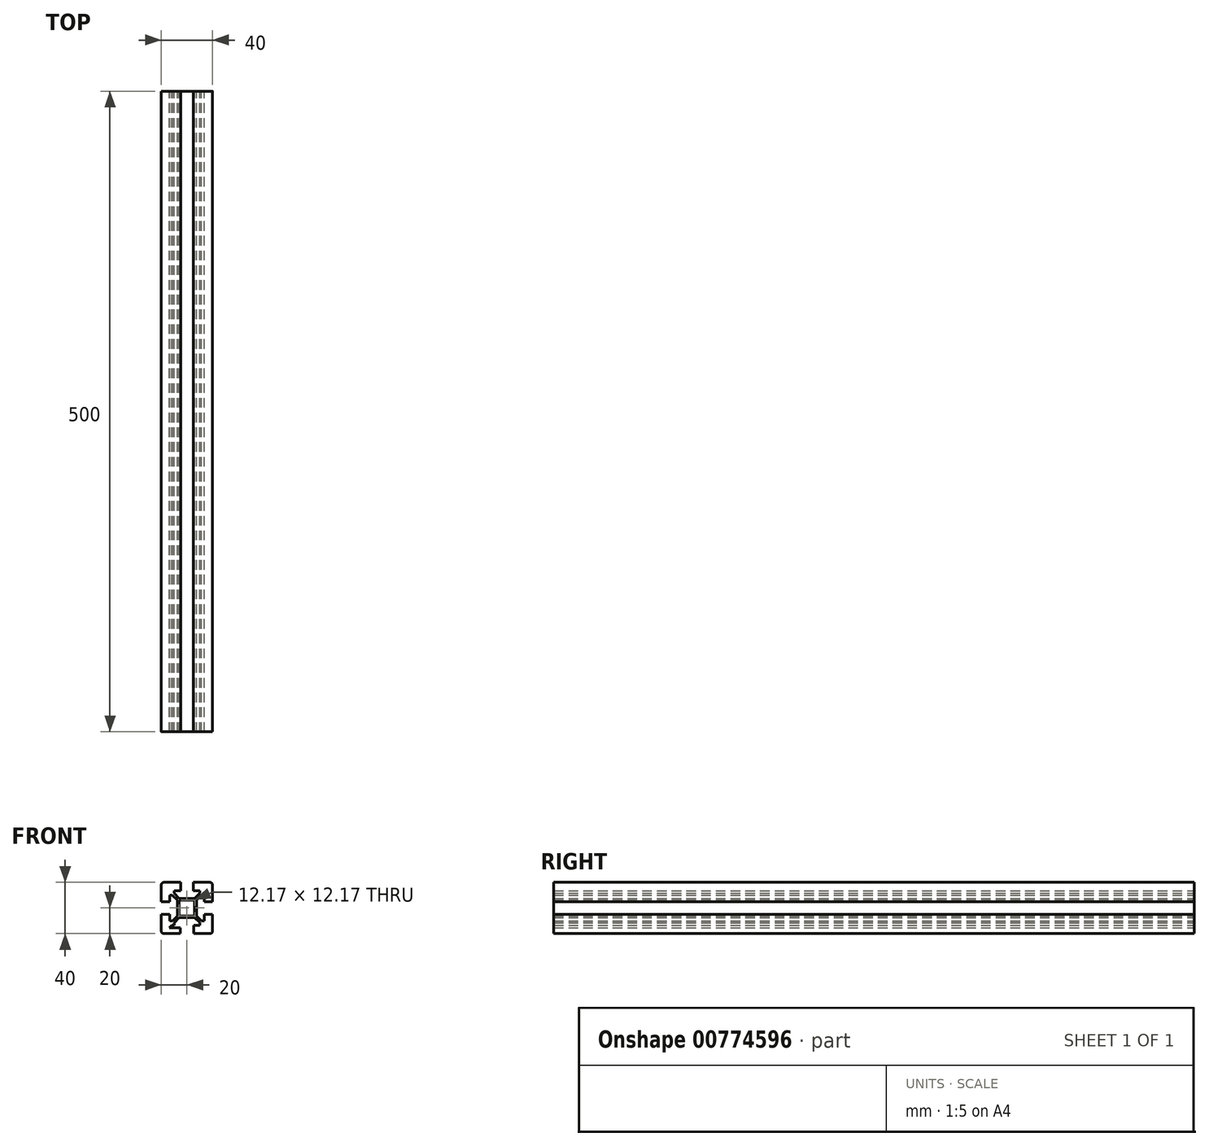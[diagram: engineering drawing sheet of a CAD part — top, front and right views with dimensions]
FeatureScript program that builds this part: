
annotation { "Feature Type Name" : "Feature", "Feature Type Description" : "" }
export const myFeature = defineFeature(function(context is Context, id is Id, definition is map)
    precondition{}
    {
        {
            var Q0;
            Q0=qCreatedBy(makeId("Front.planeOp"),FACE);
            var sketch = newSketch(context, id + "F0", { "sketchPlane" : qUnion([Q0])});
            skLineSegment(sketch, "E0.bottom", {"start": v(18, -20) * mm, "end": v(5.2, -20) * mm});
            skLineSegment(sketch, "E0.top", {"start": v(18, 20) * mm, "end": v(5, 20) * mm});
            skLineSegment(sketch, "E0.left", {"start": v(20, -18) * mm, "end": v(20, -5) * mm});
            skLineSegment(sketch, "E0.right", {"start": v(-20, -18) * mm, "end": v(-20, -5) * mm});
            skPoint(sketch, "E0.middle", {"position": v(0, 0) * mm});
            skLineSegment(sketch, "E1.bottom", {"start": v(16.63, -17.93) * mm, "end": v(5.2, -17.93) * mm});
            skLineSegment(sketch, "E1.top", {"start": v(16.58, 17.93) * mm, "end": v(5.15, 17.93) * mm});
            skLineSegment(sketch, "E1.left", {"start": v(18.05, -16.6) * mm, "end": v(18.05, -5.01) * mm});
            skLineSegment(sketch, "E1.right", {"start": v(-18.05, -16.9) * mm, "end": v(-18.05, -5.01) * mm});
            skLineSegment(sketch, "E2.bottom", {"start": v(5.5, -5.5) * mm, "end": v(-5.5, -5.5) * mm});
            skLineSegment(sketch, "E2.top", {"start": v(5.5, 5.5) * mm, "end": v(-5.5, 5.5) * mm});
            skLineSegment(sketch, "E2.left", {"start": v(5.5, -5.5) * mm, "end": v(5.5, 5.5) * mm});
            skLineSegment(sketch, "E2.right", {"start": v(-5.5, -5.5) * mm, "end": v(-5.5, 5.5) * mm});
            skLineSegment(sketch, "E3.bottom", {"start": v(6.09, -7.52) * mm, "end": v(-6.06, -7.52) * mm});
            skLineSegment(sketch, "E3.top", {"start": v(6.09, 7.52) * mm, "end": v(-6.09, 7.52) * mm});
            skLineSegment(sketch, "E3.left", {"start": v(7.48, -6.09) * mm, "end": v(7.48, 6.09) * mm});
            skLineSegment(sketch, "E3.right", {"start": v(-7.48, -6.12) * mm, "end": v(-7.48, 6.09) * mm});
            skPoint(sketch, "E4.middle", {"position": v(-20, 0) * mm});
            skLineSegment(sketch, "E5.left", {"start": v(5.2, -17.93) * mm, "end": v(5.2, -20) * mm});
            skLineSegment(sketch, "E5.right", {"start": v(-5.2, -17.93) * mm, "end": v(-5.2, -20) * mm});
            skPoint(sketch, "E5.middle", {"position": v(0, -20) * mm});
            skPoint(sketch, "E6.middle", {"position": v(20, 0) * mm});
            skPoint(sketch, "E7.middle", {"position": v(0, 20) * mm});
            skLineSegment(sketch, "E8.trimOffspring", {"start": v(-20, 5) * mm, "end": v(-20, 18) * mm});
            skLineSegment(sketch, "E9.trimOffspring", {"start": v(-18.05, 4.99) * mm, "end": v(-18.05, 10) * mm});
            skPoint(sketch, "E10.orphan", {"position": v(-21.95, 5.01) * mm});
            skPoint(sketch, "E11.orphan", {"position": v(-21.95, -4.99) * mm});
            skLineSegment(sketch, "E12.trimOffspring", {"start": v(-5, 20) * mm, "end": v(-18, 20) * mm});
            skLineSegment(sketch, "E13.trimOffspring", {"start": v(-4.85, 17.93) * mm, "end": v(-10, 17.93) * mm});
            skPoint(sketch, "E14.orphan", {"position": v(4.85, 22.07) * mm});
            skPoint(sketch, "E15.orphan", {"position": v(-5.15, 22.07) * mm});
            skLineSegment(sketch, "E16.trimOffspring", {"start": v(20, 5) * mm, "end": v(20, 18) * mm});
            skLineSegment(sketch, "E17.trimOffspring", {"start": v(18.05, 4.99) * mm, "end": v(18.05, 16.57) * mm});
            skPoint(sketch, "E18.orphan", {"position": v(21.95, -4.99) * mm});
            skPoint(sketch, "E19.orphan", {"position": v(21.95, 5.01) * mm});
            skLineSegment(sketch, "E20.trimOffspring", {"start": v(-5.2, -20) * mm, "end": v(-18, -20) * mm});
            skLineSegment(sketch, "E21.trimOffspring", {"start": v(-5.2, -17.93) * mm, "end": v(-16.28, -17.93) * mm});
            skPoint(sketch, "E22.orphan", {"position": v(-5.2, -22.07) * mm});
            skPoint(sketch, "E23.orphan", {"position": v(5.2, -22.07) * mm});
            skLineSegment(sketch, "E24", {"start": v(-14.14, 15.5) * mm, "end": v(-6.09, 7.52) * mm});
            skLineSegment(sketch, "E25", {"start": v(-7.48, 6.09) * mm, "end": v(-15.5, 14.04) * mm});
            skPoint(sketch, "E26.orphan", {"position": v(-18.05, 17.93) * mm});
            skPoint(sketch, "E27.orphan", {"position": v(-7.48, 7.52) * mm});
            skLineSegment(sketch, "E28", {"start": v(6.09, 7.52) * mm, "end": v(16.58, 17.93) * mm});
            skLineSegment(sketch, "E29", {"start": v(7.48, 6.09) * mm, "end": v(18.05, 16.57) * mm});
            skPoint(sketch, "E30.orphan", {"position": v(18.05, 17.93) * mm});
            skPoint(sketch, "E31.orphan", {"position": v(7.48, 7.52) * mm});
            skLineSegment(sketch, "E32", {"start": v(7.48, -6.09) * mm, "end": v(15.5, -14.06) * mm});
            skLineSegment(sketch, "E33", {"start": v(14.17, -15.5) * mm, "end": v(6.09, -7.52) * mm});
            skPoint(sketch, "E34.orphan", {"position": v(18.05, -17.93) * mm});
            skPoint(sketch, "E35.end.orphan", {"position": v(7.48, -7.52) * mm});
            skLineSegment(sketch, "E36", {"start": v(-15.5, -14.3) * mm, "end": v(-7.48, -6.12) * mm});
            skLineSegment(sketch, "E37", {"start": v(-6.06, -7.52) * mm, "end": v(-13.9, -15.5) * mm});
            skPoint(sketch, "E38.orphan", {"position": v(-18.05, -17.93) * mm});
            skPoint(sketch, "E39.orphan", {"position": v(-7.48, -7.52) * mm});
            skLineSegment(sketch, "E40.bottom", {"start": v(15.5, -15.5) * mm, "end": v(5.2, -15.5) * mm});
            skLineSegment(sketch, "E40.top", {"start": v(14.13, 15.5) * mm, "end": v(5, 15.5) * mm});
            skLineSegment(sketch, "E40.left", {"start": v(15.5, -15.5) * mm, "end": v(15.5, -5) * mm});
            skLineSegment(sketch, "E40.right", {"start": v(-15.5, -14.3) * mm, "end": v(-15.5, -5) * mm});
            skLineSegment(sketch, "E41.bottom", {"start": v(12.14, -13.5) * mm, "end": v(5.2, -13.5) * mm});
            skLineSegment(sketch, "E41.top", {"start": v(12.12, 13.5) * mm, "end": v(5, 13.5) * mm});
            skLineSegment(sketch, "E41.left", {"start": v(13.5, -10) * mm, "end": v(13.5, -5) * mm});
            skLineSegment(sketch, "E41.right", {"start": v(-13.5, -12.26) * mm, "end": v(-13.5, -5) * mm});
            skLineSegment(sketch, "E42.bottom", {"start": v(18.05, 10) * mm, "end": v(11.43, 10) * mm});
            skLineSegment(sketch, "E42.top", {"start": v(18.05, -10) * mm, "end": v(11.42, -10) * mm});
            skPoint(sketch, "E43.orphan", {"position": v(25.35, 10) * mm});
            skPoint(sketch, "E44.orphan", {"position": v(25.35, -10) * mm});
            skPoint(sketch, "E42.right.start.orphan", {"position": v(-25.35, 10) * mm});
            skPoint(sketch, "E45.orphan", {"position": v(-25.35, -10) * mm});
            skLineSegment(sketch, "E46", {"start": v(-20, 5) * mm, "end": v(-13.5, 5) * mm});
            skLineSegment(sketch, "E47", {"start": v(-20, -5) * mm, "end": v(-13.5, -5) * mm});
            skLineSegment(sketch, "E48", {"start": v(20, -5) * mm, "end": v(13.5, -5) * mm});
            skLineSegment(sketch, "E49", {"start": v(20, 5) * mm, "end": v(13.5, 5) * mm});
            skLineSegment(sketch, "E50.trimOffspring", {"start": v(-15.5, 5) * mm, "end": v(-15.5, 14.04) * mm});
            skLineSegment(sketch, "E51.trimOffspring", {"start": v(-13.5, 5) * mm, "end": v(-13.5, 12.06) * mm});
            skLineSegment(sketch, "E52.trimOffspring", {"start": v(13.5, 5) * mm, "end": v(13.5, 12.06) * mm});
            skLineSegment(sketch, "E53.trimOffspring", {"start": v(15.5, 5) * mm, "end": v(15.5, 14.04) * mm});
            skLineSegment(sketch, "E54.trimOffspring", {"start": v(-11.29, -10) * mm, "end": v(-18.05, -10) * mm});
            skLineSegment(sketch, "E55", {"start": v(-5, 20) * mm, "end": v(-5, 13.5) * mm});
            skLineSegment(sketch, "E56", {"start": v(5, 20) * mm, "end": v(5, 13.5) * mm});
            skLineSegment(sketch, "E57.trimOffspring", {"start": v(-5, 15.5) * mm, "end": v(-14.14, 15.5) * mm});
            skLineSegment(sketch, "E58.trimOffspring", {"start": v(-5, 13.5) * mm, "end": v(-12.12, 13.5) * mm});
            skLineSegment(sketch, "E59.left", {"start": v(10, -20) * mm, "end": v(10, -11.38) * mm});
            skLineSegment(sketch, "E59.right", {"start": v(-10, -20) * mm, "end": v(-10, -11.53) * mm});
            skPoint(sketch, "E60.orphan", {"position": v(-10, 43.24) * mm});
            skPoint(sketch, "E61.orphan", {"position": v(10, 43.24) * mm});
            skPoint(sketch, "E59.bottom.end.orphan", {"position": v(-10, -43.24) * mm});
            skPoint(sketch, "E59.bottom.start.orphan", {"position": v(10, -43.24) * mm});
            skLineSegment(sketch, "E62", {"start": v(-18.05, 17.93) * mm, "end": v(-18.05, 10) * mm});
            skLineSegment(sketch, "E63", {"start": v(-18.05, 17.93) * mm, "end": v(-10, 17.93) * mm});
            skLineSegment(sketch, "E64.trimOffspring", {"start": v(-10, 11.4) * mm, "end": v(-10, 20) * mm});
            skLineSegment(sketch, "E65.trimOffspring", {"start": v(-11.43, 10) * mm, "end": v(-18.05, 10) * mm});
            skPoint(sketch, "E66.orphan", {"position": v(-13.5, 13.5) * mm});
            skLineSegment(sketch, "E67", {"start": v(-5.2, -17.93) * mm, "end": v(-5.2, -15.5) * mm});
            skLineSegment(sketch, "E68", {"start": v(5.2, -17.93) * mm, "end": v(5.2, -15.5) * mm});
            skLineSegment(sketch, "E69", {"start": v(5.2, -15.5) * mm, "end": v(5.2, -13.5) * mm});
            skLineSegment(sketch, "E70", {"start": v(-5.2, -15.5) * mm, "end": v(-5.2, -13.5) * mm});
            skLineSegment(sketch, "E71.trimOffspring", {"start": v(-5.2, -13.5) * mm, "end": v(-11.94, -13.5) * mm});
            skLineSegment(sketch, "E72.trimOffspring", {"start": v(-5.2, -15.5) * mm, "end": v(-13.9, -15.5) * mm});
            skLineSegment(sketch, "E73.trimOffspring", {"start": v(10, 11.4) * mm, "end": v(10, 20) * mm});
            skPoint(sketch, "E74.orphan", {"position": v(13.5, -13.5) * mm});
            skPoint(sketch, "E75.orphan", {"position": v(-15.5, -15.5) * mm});
            skPoint(sketch, "E76.orphan", {"position": v(-13.5, -13.5) * mm});
            skPoint(sketch, "E77.orphan", {"position": v(13.5, 13.5) * mm});
            skPoint(sketch, "E78.orphan", {"position": v(15.5, 15.5) * mm});
            skPoint(sketch, "E79.orphan", {"position": v(-15.5, 15.5) * mm});
            skPoint(sketch, "E80.visualSharp", {"position": v(-20, 20) * mm});
            skArc(sketch, "E80.filletArc", {"start": v(-18, 20) * mm, "mid": v(-19.41, 19.41) * mm, "end": v(-20, 18) * mm});
            skPoint(sketch, "E81.visualSharp", {"position": v(20, 20) * mm});
            skArc(sketch, "E81.filletArc", {"start": v(20, 18) * mm, "mid": v(19.41, 19.41) * mm, "end": v(18, 20) * mm});
            skPoint(sketch, "E82.visualSharp", {"position": v(20, -20) * mm});
            skArc(sketch, "E82.filletArc", {"start": v(18, -20) * mm, "mid": v(19.41, -19.41) * mm, "end": v(20, -18) * mm});
            skPoint(sketch, "E83.visualSharp", {"position": v(-20, -20) * mm});
            skArc(sketch, "E83.filletArc", {"start": v(-20, -18) * mm, "mid": v(-19.41, -19.41) * mm, "end": v(-18, -20) * mm});
            skSolve(sketch);
        }
        {
            var Q0;
            {var subQ1=sQuery(id+"F0.wireOp",EDGE,"E16.trimOffspring");Q0=makeQuery(id+"F0.imprint","IMPRINT",FACE,{"disambiguationData":[TD([[makeQuery(id+"F0.imprint","IMPRINT",EDGE,{"derivedFrom":subQ1}),1.0]])]});}
            var Q1;
            {var subQ0=sQuery(id+"F0.wireOp",EDGE,"E52.trimOffspring");var subQ1=sQuery(id+"F0.wireOp",EDGE,"E29");var subQ2=makeQuery(id+"F0.imprint","INTERSECT",VERTEX,{"derivedFrom":[subQ1,subQ0]});Q1=makeQuery(id+"F0.imprint","IMPRINT",FACE,{"disambiguationData":[TD([[makeQuery(id+"F0.imprint","IMPRINT",EDGE,{"disambiguationData":[TD([[subQ2,-1.0]])],"derivedFrom":subQ1}),-1.0]])]});}
            var Q2;
            {var subQ0=sQuery(id+"F0.wireOp",EDGE,"E59.left");var subQ1=sQuery(id+"F0.wireOp",EDGE,"E40.bottom");var subQ2=makeQuery(id+"F0.imprint","INTERSECT",VERTEX,{"derivedFrom":[subQ1,subQ0]});Q2=makeQuery(id+"F0.imprint","IMPRINT",FACE,{"disambiguationData":[TD([[makeQuery(id+"F0.imprint","IMPRINT",EDGE,{"disambiguationData":[TD([[subQ2,-1.0]])],"derivedFrom":subQ1}),-1.0]])]});}
            var Q3;
            {var subQ5=sQuery(id+"F0.wireOp",EDGE,"E32");var subQ9=sQuery(id+"F0.wireOp",EDGE,"E42.top");var subQ11=makeQuery(id+"F0.imprint","INTERSECT",VERTEX,{"derivedFrom":[subQ5,subQ9]});Q3=makeQuery(id+"F0.imprint","IMPRINT",FACE,{"disambiguationData":[TD([[makeQuery(id+"F0.imprint","IMPRINT",EDGE,{"disambiguationData":[TD([[subQ11,-1.0]])],"derivedFrom":subQ5}),-1.0]])]});}
            var Q4;
            {var subQ0=sQuery(id+"F0.wireOp",EDGE,"E40.right");var subQ1=sQuery(id+"F0.wireOp",EDGE,"E36");var subQ2=makeQuery(id+"F0.imprint","INTERSECT",VERTEX,{"derivedFrom":[subQ1,subQ0]});Q4=makeQuery(id+"F0.imprint","IMPRINT",FACE,{"disambiguationData":[TD([[makeQuery(id+"F0.imprint","IMPRINT",EDGE,{"disambiguationData":[TD([[subQ2,-1.0]])],"derivedFrom":subQ1}),1.0]])]});}
            var Q5;
            {var subQ0=sQuery(id+"F0.wireOp",EDGE,"E37");var subQ1=sQuery(id+"F0.wireOp",EDGE,"E21.trimOffspring");var subQ2=makeQuery(id+"F0.imprint","INTERSECT",VERTEX,{"derivedFrom":[subQ1,subQ0]});Q5=makeQuery(id+"F0.imprint","IMPRINT",FACE,{"disambiguationData":[TD([[makeQuery(id+"F0.imprint","IMPRINT",EDGE,{"disambiguationData":[TD([[subQ2,1.0]])],"derivedFrom":subQ1}),-1.0]])]});}
            var Q6;
            {var subQ0=sQuery(id+"F0.wireOp",EDGE,"E59.left");var subQ1=sQuery(id+"F0.wireOp",EDGE,"E28");var subQ2=makeQuery(id+"F0.imprint","INTERSECT",VERTEX,{"derivedFrom":[subQ1,subQ0]});Q6=makeQuery(id+"F0.imprint","IMPRINT",FACE,{"disambiguationData":[TD([[makeQuery(id+"F0.imprint","IMPRINT",EDGE,{"disambiguationData":[TD([[subQ2,-1.0]])],"derivedFrom":subQ1}),1.0]])]});}
            var Q7;
            {var subQ3=sQuery(id+"F0.wireOp",EDGE,"E36");var subQ5=sQuery(id+"F0.wireOp",EDGE,"E54.trimOffspring");var subQ6=makeQuery(id+"F0.imprint","INTERSECT",VERTEX,{"derivedFrom":[subQ3,subQ5]});Q7=makeQuery(id+"F0.imprint","IMPRINT",FACE,{"disambiguationData":[TD([[makeQuery(id+"F0.imprint","IMPRINT",EDGE,{"disambiguationData":[TD([[subQ6,1.0]])],"derivedFrom":subQ3}),-1.0]])]});}
            var Q8;
            {var subQ3=sQuery(id+"F0.wireOp",EDGE,"E46");var subQ5=sQuery(id+"F0.wireOp",EDGE,"E50.trimOffspring");var subQ7=makeQuery(id+"F0.imprint","INTERSECT",VERTEX,{"derivedFrom":[subQ3,subQ5]});Q8=makeQuery(id+"F0.imprint","IMPRINT",FACE,{"disambiguationData":[TD([[makeQuery(id+"F0.imprint","IMPRINT",EDGE,{"disambiguationData":[TD([[subQ7,1.0]])],"derivedFrom":subQ3}),1.0]])]});}
            var Q9;
            {var subQ0=sQuery(id+"F0.wireOp",EDGE,"E52.trimOffspring");var subQ1=sQuery(id+"F0.wireOp",EDGE,"E42.bottom");var subQ2=makeQuery(id+"F0.imprint","INTERSECT",VERTEX,{"derivedFrom":[subQ1,subQ0]});Q9=makeQuery(id+"F0.imprint","IMPRINT",FACE,{"disambiguationData":[TD([[makeQuery(id+"F0.imprint","IMPRINT",EDGE,{"disambiguationData":[TD([[subQ2,1.0]])],"derivedFrom":subQ1}),1.0]])]});}
            var Q10;
            {var subQ0=sQuery(id+"F0.wireOp",EDGE,"E28");var subQ1=sQuery(id+"F0.wireOp",EDGE,"E1.top");var subQ2=makeQuery(id+"F0.imprint","INTERSECT",VERTEX,{"derivedFrom":[subQ1,subQ0]});Q10=makeQuery(id+"F0.imprint","IMPRINT",FACE,{"disambiguationData":[TD([[makeQuery(id+"F0.imprint","IMPRINT",EDGE,{"disambiguationData":[TD([[subQ2,-1.0]])],"derivedFrom":subQ1}),1.0]])]});}
            var Q11;
            {var subQ13=sQuery(id+"F0.wireOp",EDGE,"E0.left");Q11=makeQuery(id+"F0.imprint","IMPRINT",FACE,{"disambiguationData":[TD([[makeQuery(id+"F0.imprint","IMPRINT",EDGE,{"derivedFrom":subQ13}),1.0]])]});}
            var Q12;
            {var subQ1=sQuery(id+"F0.wireOp",EDGE,"E0.right");Q12=makeQuery(id+"F0.imprint","IMPRINT",FACE,{"disambiguationData":[TD([[makeQuery(id+"F0.imprint","IMPRINT",EDGE,{"derivedFrom":subQ1}),-1.0]])]});}
            var Q13;
            {var subQ0=sQuery(id+"F0.wireOp",EDGE,"E33");var subQ1=sQuery(id+"F0.wireOp",EDGE,"E1.bottom");var subQ2=makeQuery(id+"F0.imprint","INTERSECT",VERTEX,{"derivedFrom":[subQ1,subQ0]});Q13=makeQuery(id+"F0.imprint","IMPRINT",FACE,{"disambiguationData":[TD([[makeQuery(id+"F0.imprint","IMPRINT",EDGE,{"disambiguationData":[TD([[subQ2,-1.0]])],"derivedFrom":subQ1}),-1.0]])]});}
            var Q14;
            {var subQ0=sQuery(id+"F0.wireOp",EDGE,"E41.left");var subQ1=sQuery(id+"F0.wireOp",EDGE,"E32");var subQ2=makeQuery(id+"F0.imprint","INTERSECT",VERTEX,{"derivedFrom":[subQ1,subQ0]});Q14=makeQuery(id+"F0.imprint","IMPRINT",FACE,{"disambiguationData":[TD([[makeQuery(id+"F0.imprint","IMPRINT",EDGE,{"disambiguationData":[TD([[subQ2,-1.0]])],"derivedFrom":subQ1}),1.0]])]});}
            var Q15;
            {var subQ3=sQuery(id+"F0.wireOp",EDGE,"E59.left");var subQ8=sQuery(id+"F0.wireOp",EDGE,"E28");var subQ11=makeQuery(id+"F0.imprint","INTERSECT",VERTEX,{"derivedFrom":[subQ8,subQ3]});Q15=makeQuery(id+"F0.imprint","IMPRINT",FACE,{"disambiguationData":[TD([[makeQuery(id+"F0.imprint","IMPRINT",EDGE,{"disambiguationData":[TD([[subQ11,-1.0]])],"derivedFrom":subQ8}),-1.0]])]});}
            var Q16;
            {var subQ0=sQuery(id+"F0.wireOp",EDGE,"E3.left");Q16=makeQuery(id+"F0.imprint","IMPRINT",FACE,{"disambiguationData":[TD([[makeQuery(id+"F0.imprint","IMPRINT",EDGE,{"derivedFrom":subQ0}),-1.0]])]});}
            var Q17;
            {var subQ0=sQuery(id+"F0.wireOp",EDGE,"E3.top");Q17=makeQuery(id+"F0.imprint","IMPRINT",FACE,{"disambiguationData":[TD([[makeQuery(id+"F0.imprint","IMPRINT",EDGE,{"derivedFrom":subQ0}),-1.0]])]});}
            var Q18;
            {var subQ0=sQuery(id+"F0.wireOp",EDGE,"E47");var subQ1=sQuery(id+"F0.wireOp",EDGE,"E40.right");var subQ2=makeQuery(id+"F0.imprint","INTERSECT",VERTEX,{"derivedFrom":[subQ1,subQ0]});Q18=makeQuery(id+"F0.imprint","IMPRINT",FACE,{"disambiguationData":[TD([[makeQuery(id+"F0.imprint","IMPRINT",EDGE,{"disambiguationData":[TD([[subQ2,1.0]])],"derivedFrom":subQ1}),-1.0]])]});}
            var Q19;
            {var subQ1=sQuery(id+"F0.wireOp",EDGE,"E8.trimOffspring");Q19=makeQuery(id+"F0.imprint","IMPRINT",FACE,{"disambiguationData":[TD([[makeQuery(id+"F0.imprint","IMPRINT",EDGE,{"derivedFrom":subQ1}),-1.0]])]});}
            var Q20;
            {var subQ0=sQuery(id+"F0.wireOp",EDGE,"E36");var subQ1=sQuery(id+"F0.wireOp",EDGE,"E1.right");var subQ2=makeQuery(id+"F0.imprint","INTERSECT",VERTEX,{"derivedFrom":[subQ1,subQ0]});Q20=makeQuery(id+"F0.imprint","IMPRINT",FACE,{"disambiguationData":[TD([[makeQuery(id+"F0.imprint","IMPRINT",EDGE,{"disambiguationData":[TD([[subQ2,-1.0]])],"derivedFrom":subQ1}),-1.0]])]});}
            var Q21;
            {var subQ0=sQuery(id+"F0.wireOp",EDGE,"E32");var subQ1=sQuery(id+"F0.wireOp",EDGE,"E1.left");var subQ2=makeQuery(id+"F0.imprint","INTERSECT",VERTEX,{"derivedFrom":[subQ1,subQ0]});Q21=makeQuery(id+"F0.imprint","IMPRINT",FACE,{"disambiguationData":[TD([[makeQuery(id+"F0.imprint","IMPRINT",EDGE,{"disambiguationData":[TD([[subQ2,-1.0]])],"derivedFrom":subQ1}),1.0]])]});}
            var Q22;
            {var subQ0=sQuery(id+"F0.wireOp",EDGE,"E3.right");Q22=makeQuery(id+"F0.imprint","IMPRINT",FACE,{"disambiguationData":[TD([[makeQuery(id+"F0.imprint","IMPRINT",EDGE,{"derivedFrom":subQ0}),1.0]])]});}
            var Q23;
            {var subQ0=sQuery(id+"F0.wireOp",EDGE,"E48");var subQ1=sQuery(id+"F0.wireOp",EDGE,"E40.left");var subQ2=makeQuery(id+"F0.imprint","INTERSECT",VERTEX,{"derivedFrom":[subQ1,subQ0]});Q23=makeQuery(id+"F0.imprint","IMPRINT",FACE,{"disambiguationData":[TD([[makeQuery(id+"F0.imprint","IMPRINT",EDGE,{"disambiguationData":[TD([[subQ2,1.0]])],"derivedFrom":subQ1}),1.0]])]});}
            var Q24;
            {var subQ0=sQuery(id+"F0.wireOp",EDGE,"E56");var subQ1=sQuery(id+"F0.wireOp",EDGE,"E40.top");var subQ2=makeQuery(id+"F0.imprint","INTERSECT",VERTEX,{"derivedFrom":[subQ1,subQ0]});Q24=makeQuery(id+"F0.imprint","IMPRINT",FACE,{"disambiguationData":[TD([[makeQuery(id+"F0.imprint","IMPRINT",EDGE,{"disambiguationData":[TD([[subQ2,1.0]])],"derivedFrom":subQ1}),1.0]])]});}
            var Q25;
            {var subQ1=sQuery(id+"F0.wireOp",EDGE,"E3.bottom");Q25=makeQuery(id+"F0.imprint","IMPRINT",FACE,{"disambiguationData":[TD([[makeQuery(id+"F0.imprint","IMPRINT",EDGE,{"derivedFrom":subQ1}),1.0]])]});}
            var Q26;
            {var subQ0=sQuery(id+"F0.wireOp",EDGE,"E40.bottom");var subQ1=sQuery(id+"F0.wireOp",EDGE,"E33");var subQ2=makeQuery(id+"F0.imprint","INTERSECT",VERTEX,{"derivedFrom":[subQ1,subQ0]});Q26=makeQuery(id+"F0.imprint","IMPRINT",FACE,{"disambiguationData":[TD([[makeQuery(id+"F0.imprint","IMPRINT",EDGE,{"disambiguationData":[TD([[subQ2,-1.0]])],"derivedFrom":subQ1}),1.0]])]});}
            var Q27;
            {var subQ0=sQuery(id+"F0.wireOp",EDGE,"E41.top");var subQ1=sQuery(id+"F0.wireOp",EDGE,"E28");var subQ2=makeQuery(id+"F0.imprint","INTERSECT",VERTEX,{"derivedFrom":[subQ1,subQ0]});Q27=makeQuery(id+"F0.imprint","IMPRINT",FACE,{"disambiguationData":[TD([[makeQuery(id+"F0.imprint","IMPRINT",EDGE,{"disambiguationData":[TD([[subQ2,-1.0]])],"derivedFrom":subQ1}),1.0]])]});}
            var Q28;
            {var subQ0=sQuery(id+"F0.wireOp",EDGE,"E41.bottom");var subQ1=sQuery(id+"F0.wireOp",EDGE,"E37");var subQ2=makeQuery(id+"F0.imprint","INTERSECT",VERTEX,{"derivedFrom":[subQ1,subQ0]});Q28=makeQuery(id+"F0.imprint","IMPRINT",FACE,{"disambiguationData":[TD([[makeQuery(id+"F0.imprint","IMPRINT",EDGE,{"disambiguationData":[TD([[subQ2,-1.0]])],"derivedFrom":subQ1}),1.0]])]});}
            var Q29;
            {var subQ4=sQuery(id+"F0.wireOp",EDGE,"E56");var subQ6=sQuery(id+"F0.wireOp",EDGE,"E0.top");var subQ7=makeQuery(id+"F0.imprint","INTERSECT",VERTEX,{"derivedFrom":[subQ6,subQ4]});Q29=makeQuery(id+"F0.imprint","IMPRINT",FACE,{"disambiguationData":[TD([[makeQuery(id+"F0.imprint","IMPRINT",EDGE,{"disambiguationData":[TD([[subQ7,1.0]])],"derivedFrom":subQ6}),1.0]])]});}
            var Q30;
            {var subQ0=sQuery(id+"F0.wireOp",EDGE,"E29");var subQ1=sQuery(id+"F0.wireOp",EDGE,"E17.trimOffspring");var subQ2=makeQuery(id+"F0.imprint","INTERSECT",VERTEX,{"derivedFrom":[subQ1,subQ0]});Q30=makeQuery(id+"F0.imprint","IMPRINT",FACE,{"disambiguationData":[TD([[makeQuery(id+"F0.imprint","IMPRINT",EDGE,{"disambiguationData":[TD([[subQ2,1.0]])],"derivedFrom":subQ1}),1.0]])]});}
            var Q31;
            {var subQ0=sQuery(id+"F0.wireOp",EDGE,"E58.trimOffspring");var subQ1=sQuery(id+"F0.wireOp",EDGE,"E55");var subQ2=makeQuery(id+"F0.imprint","INTERSECT",VERTEX,{"derivedFrom":[subQ1,subQ0]});Q31=makeQuery(id+"F0.imprint","IMPRINT",FACE,{"disambiguationData":[TD([[makeQuery(id+"F0.imprint","IMPRINT",EDGE,{"disambiguationData":[TD([[subQ2,1.0]])],"derivedFrom":subQ1}),-1.0]])]});}
            var Q32;
            {var subQ3=sQuery(id+"F0.wireOp",EDGE,"E55");var subQ5=sQuery(id+"F0.wireOp",EDGE,"E57.trimOffspring");var subQ6=makeQuery(id+"F0.imprint","INTERSECT",VERTEX,{"derivedFrom":[subQ3,subQ5]});Q32=makeQuery(id+"F0.imprint","IMPRINT",FACE,{"disambiguationData":[TD([[makeQuery(id+"F0.imprint","IMPRINT",EDGE,{"disambiguationData":[TD([[subQ6,1.0]])],"derivedFrom":subQ3}),-1.0]])]});}
            var Q33;
            Q33=makeQuery(id+"F0.imprint","IMPRINT",FACE,{"disambiguationData":[TD([[makeQuery(id+"F0.imprint","IMPRINT",EDGE,{"derivedFrom":sQuery(id+"F0.wireOp",EDGE,"E2.bottom")}),1.0]])]});
            var Q34;
            {var subQ0=sQuery(id+"F0.wireOp",EDGE,"E51.trimOffspring");var subQ1=sQuery(id+"F0.wireOp",EDGE,"E46");var subQ2=makeQuery(id+"F0.imprint","INTERSECT",VERTEX,{"derivedFrom":[subQ1,subQ0]});Q34=makeQuery(id+"F0.imprint","IMPRINT",FACE,{"disambiguationData":[TD([[makeQuery(id+"F0.imprint","IMPRINT",EDGE,{"disambiguationData":[TD([[subQ2,1.0]])],"derivedFrom":subQ1}),1.0]])]});}
            var Q35;
            {var subQ0=sQuery(id+"F0.wireOp",EDGE,"E42.bottom");var subQ1=sQuery(id+"F0.wireOp",EDGE,"E28");var subQ2=makeQuery(id+"F0.imprint","INTERSECT",VERTEX,{"derivedFrom":[subQ1,subQ0]});Q35=makeQuery(id+"F0.imprint","IMPRINT",FACE,{"disambiguationData":[TD([[makeQuery(id+"F0.imprint","IMPRINT",EDGE,{"disambiguationData":[TD([[subQ2,-1.0]])],"derivedFrom":subQ1}),-1.0]])]});}
            var Q36;
            Q36=makeQuery(id+"F0.imprint","IMPRINT",FACE,{"disambiguationData":[TD([[makeQuery(id+"F0.imprint","IMPRINT",EDGE,{"derivedFrom":sQuery(id+"F0.wireOp",EDGE,"E2.bottom")}),-1.0]])]});
            var Q37;
            {var subQ0=sQuery(id+"F0.wireOp",EDGE,"E50.trimOffspring");var subQ1=sQuery(id+"F0.wireOp",EDGE,"E25");var subQ2=makeQuery(id+"F0.imprint","INTERSECT",VERTEX,{"derivedFrom":[subQ1,subQ0]});Q37=makeQuery(id+"F0.imprint","IMPRINT",FACE,{"disambiguationData":[TD([[makeQuery(id+"F0.imprint","IMPRINT",EDGE,{"disambiguationData":[TD([[subQ2,1.0]])],"derivedFrom":subQ1}),1.0]])]});}
            var Q38;
            {var subQ0=sQuery(id+"F0.wireOp",EDGE,"E58.trimOffspring");var subQ1=sQuery(id+"F0.wireOp",EDGE,"E24");var subQ2=makeQuery(id+"F0.imprint","INTERSECT",VERTEX,{"derivedFrom":[subQ1,subQ0]});Q38=makeQuery(id+"F0.imprint","IMPRINT",FACE,{"disambiguationData":[TD([[makeQuery(id+"F0.imprint","IMPRINT",EDGE,{"disambiguationData":[TD([[subQ2,-1.0]])],"derivedFrom":subQ1}),1.0]])]});}
            var Q39;
            {var subQ0=sQuery(id+"F0.wireOp",EDGE,"E59.right");var subQ1=sQuery(id+"F0.wireOp",EDGE,"E37");var subQ2=makeQuery(id+"F0.imprint","INTERSECT",VERTEX,{"derivedFrom":[subQ1,subQ0]});Q39=makeQuery(id+"F0.imprint","IMPRINT",FACE,{"disambiguationData":[TD([[makeQuery(id+"F0.imprint","IMPRINT",EDGE,{"disambiguationData":[TD([[subQ2,-1.0]])],"derivedFrom":subQ1}),1.0]])]});}
            var Q40;
            {var subQ0=sQuery(id+"F0.wireOp",EDGE,"E55");var subQ1=sQuery(id+"F0.wireOp",EDGE,"E12.trimOffspring");var subQ2=makeQuery(id+"F0.imprint","INTERSECT",VERTEX,{"derivedFrom":[subQ1,subQ0]});Q40=makeQuery(id+"F0.imprint","IMPRINT",FACE,{"disambiguationData":[TD([[makeQuery(id+"F0.imprint","IMPRINT",EDGE,{"disambiguationData":[TD([[subQ2,-1.0]])],"derivedFrom":subQ1}),1.0]])]});}
            var Q41;
            {var subQ0=sQuery(id+"F0.wireOp",EDGE,"E42.bottom");var subQ1=sQuery(id+"F0.wireOp",EDGE,"E17.trimOffspring");var subQ2=makeQuery(id+"F0.imprint","INTERSECT",VERTEX,{"derivedFrom":[subQ1,subQ0]});Q41=makeQuery(id+"F0.imprint","IMPRINT",FACE,{"disambiguationData":[TD([[makeQuery(id+"F0.imprint","IMPRINT",EDGE,{"disambiguationData":[TD([[subQ2,1.0]])],"derivedFrom":subQ1}),1.0]])]});}
            var Q42;
            {var subQ0=sQuery(id+"F0.wireOp",EDGE,"E41.bottom");var subQ1=sQuery(id+"F0.wireOp",EDGE,"E33");var subQ2=makeQuery(id+"F0.imprint","INTERSECT",VERTEX,{"derivedFrom":[subQ1,subQ0]});Q42=makeQuery(id+"F0.imprint","IMPRINT",FACE,{"disambiguationData":[TD([[makeQuery(id+"F0.imprint","IMPRINT",EDGE,{"disambiguationData":[TD([[subQ2,-1.0]])],"derivedFrom":subQ1}),1.0]])]});}
            var Q43;
            {var subQ0=sQuery(id+"F0.wireOp",EDGE,"E54.trimOffspring");var subQ1=sQuery(id+"F0.wireOp",EDGE,"E36");var subQ2=makeQuery(id+"F0.imprint","INTERSECT",VERTEX,{"derivedFrom":[subQ1,subQ0]});Q43=makeQuery(id+"F0.imprint","IMPRINT",FACE,{"disambiguationData":[TD([[makeQuery(id+"F0.imprint","IMPRINT",EDGE,{"disambiguationData":[TD([[subQ2,1.0]])],"derivedFrom":subQ1}),1.0]])]});}
            var Q44;
            {var subQ0=sQuery(id+"F0.wireOp",EDGE,"E54.trimOffspring");var subQ1=sQuery(id+"F0.wireOp",EDGE,"E37");var subQ2=makeQuery(id+"F0.imprint","INTERSECT",VERTEX,{"derivedFrom":[subQ1,subQ0]});Q44=makeQuery(id+"F0.imprint","IMPRINT",FACE,{"disambiguationData":[TD([[makeQuery(id+"F0.imprint","IMPRINT",EDGE,{"disambiguationData":[TD([[subQ2,-1.0]])],"derivedFrom":subQ1}),-1.0]])]});}
            var Q45;
            {var subQ0=sQuery(id+"F0.wireOp",EDGE,"E5.left");Q45=makeQuery(id+"F0.imprint","IMPRINT",FACE,{"disambiguationData":[TD([[makeQuery(id+"F0.imprint","IMPRINT",EDGE,{"derivedFrom":subQ0}),1.0]])]});}
            var Q46;
            {var subQ0=sQuery(id+"F0.wireOp",EDGE,"E51.trimOffspring");var subQ1=sQuery(id+"F0.wireOp",EDGE,"E25");var subQ2=makeQuery(id+"F0.imprint","INTERSECT",VERTEX,{"derivedFrom":[subQ1,subQ0]});Q46=makeQuery(id+"F0.imprint","IMPRINT",FACE,{"disambiguationData":[TD([[makeQuery(id+"F0.imprint","IMPRINT",EDGE,{"disambiguationData":[TD([[subQ2,1.0]])],"derivedFrom":subQ1}),1.0]])]});}
            var Q47;
            {var subQ0=sQuery(id+"F0.wireOp",EDGE,"E42.bottom");var subQ1=sQuery(id+"F0.wireOp",EDGE,"E29");var subQ2=makeQuery(id+"F0.imprint","INTERSECT",VERTEX,{"derivedFrom":[subQ1,subQ0]});Q47=makeQuery(id+"F0.imprint","IMPRINT",FACE,{"disambiguationData":[TD([[makeQuery(id+"F0.imprint","IMPRINT",EDGE,{"disambiguationData":[TD([[subQ2,-1.0]])],"derivedFrom":subQ1}),-1.0]])]});}
            var Q48;
            {var subQ0=sQuery(id+"F0.wireOp",EDGE,"E5.right");Q48=makeQuery(id+"F0.imprint","IMPRINT",FACE,{"disambiguationData":[TD([[makeQuery(id+"F0.imprint","IMPRINT",EDGE,{"derivedFrom":subQ0}),-1.0]])]});}
            var Q49;
            {var subQ0=sQuery(id+"F0.wireOp",EDGE,"E42.top");var subQ1=sQuery(id+"F0.wireOp",EDGE,"E33");var subQ2=makeQuery(id+"F0.imprint","INTERSECT",VERTEX,{"derivedFrom":[subQ1,subQ0]});Q49=makeQuery(id+"F0.imprint","IMPRINT",FACE,{"disambiguationData":[TD([[makeQuery(id+"F0.imprint","IMPRINT",EDGE,{"disambiguationData":[TD([[subQ2,1.0]])],"derivedFrom":subQ1}),-1.0]])]});}
            var Q50;
            {var subQ0=sQuery(id+"F0.wireOp",EDGE,"E54.trimOffspring");var subQ1=sQuery(id+"F0.wireOp",EDGE,"E36");var subQ2=makeQuery(id+"F0.imprint","INTERSECT",VERTEX,{"derivedFrom":[subQ1,subQ0]});Q50=makeQuery(id+"F0.imprint","IMPRINT",FACE,{"disambiguationData":[TD([[makeQuery(id+"F0.imprint","IMPRINT",EDGE,{"disambiguationData":[TD([[subQ2,-1.0]])],"derivedFrom":subQ1}),-1.0]])]});}
            var Q51;
            {var subQ0=sQuery(id+"F0.wireOp",EDGE,"E59.left");var subQ1=sQuery(id+"F0.wireOp",EDGE,"E29");var subQ2=makeQuery(id+"F0.imprint","INTERSECT",VERTEX,{"derivedFrom":[subQ1,subQ0]});Q51=makeQuery(id+"F0.imprint","IMPRINT",FACE,{"disambiguationData":[TD([[makeQuery(id+"F0.imprint","IMPRINT",EDGE,{"disambiguationData":[TD([[subQ2,-1.0]])],"derivedFrom":subQ1}),1.0]])]});}
            var Q52;
            {var subQ0=sQuery(id+"F0.wireOp",EDGE,"E59.left");var subQ1=sQuery(id+"F0.wireOp",EDGE,"E32");var subQ2=makeQuery(id+"F0.imprint","INTERSECT",VERTEX,{"derivedFrom":[subQ1,subQ0]});Q52=makeQuery(id+"F0.imprint","IMPRINT",FACE,{"disambiguationData":[TD([[makeQuery(id+"F0.imprint","IMPRINT",EDGE,{"disambiguationData":[TD([[subQ2,-1.0]])],"derivedFrom":subQ1}),-1.0]])]});}
            var Q53;
            {var subQ0=sQuery(id+"F0.wireOp",EDGE,"E42.top");var subQ1=sQuery(id+"F0.wireOp",EDGE,"E32");var subQ2=makeQuery(id+"F0.imprint","INTERSECT",VERTEX,{"derivedFrom":[subQ1,subQ0]});Q53=makeQuery(id+"F0.imprint","IMPRINT",FACE,{"disambiguationData":[TD([[makeQuery(id+"F0.imprint","IMPRINT",EDGE,{"disambiguationData":[TD([[subQ2,-1.0]])],"derivedFrom":subQ1}),1.0]])]});}
            var Q54;
            {var subQ0=sQuery(id+"F0.wireOp",EDGE,"E57.trimOffspring");var subQ1=sQuery(id+"F0.wireOp",EDGE,"E24");var subQ2=makeQuery(id+"F0.imprint","INTERSECT",VERTEX,{"derivedFrom":[subQ1,subQ0]});Q54=makeQuery(id+"F0.imprint","IMPRINT",FACE,{"disambiguationData":[TD([[makeQuery(id+"F0.imprint","IMPRINT",EDGE,{"disambiguationData":[TD([[subQ2,-1.0]])],"derivedFrom":subQ1}),1.0]])]});}
            var Q55;
            {var subQ5=sQuery(id+"F0.wireOp",EDGE,"E41.left");var subQ8=sQuery(id+"F0.wireOp",EDGE,"E32");var subQ9=makeQuery(id+"F0.imprint","INTERSECT",VERTEX,{"derivedFrom":[subQ8,subQ5]});Q55=makeQuery(id+"F0.imprint","IMPRINT",FACE,{"disambiguationData":[TD([[makeQuery(id+"F0.imprint","IMPRINT",EDGE,{"disambiguationData":[TD([[subQ9,-1.0]])],"derivedFrom":subQ8}),-1.0]])]});}
            var Q56;
            {var subQ1=sQuery(id+"F0.wireOp",EDGE,"E41.top");var subQ3=sQuery(id+"F0.wireOp",EDGE,"E28");var subQ4=makeQuery(id+"F0.imprint","INTERSECT",VERTEX,{"derivedFrom":[subQ3,subQ1]});Q56=makeQuery(id+"F0.imprint","IMPRINT",FACE,{"disambiguationData":[TD([[makeQuery(id+"F0.imprint","IMPRINT",EDGE,{"disambiguationData":[TD([[subQ4,-1.0]])],"derivedFrom":subQ3}),-1.0]])]});}
            var Q57;
            {var subQ0=sQuery(id+"F0.wireOp",EDGE,"E40.right");var subQ7=sQuery(id+"F0.wireOp",EDGE,"E36");var subQ8=makeQuery(id+"F0.imprint","INTERSECT",VERTEX,{"derivedFrom":[subQ7,subQ0]});Q57=makeQuery(id+"F0.imprint","IMPRINT",FACE,{"disambiguationData":[TD([[makeQuery(id+"F0.imprint","IMPRINT",EDGE,{"disambiguationData":[TD([[subQ8,-1.0]])],"derivedFrom":subQ7}),-1.0]])]});}
            extrude(context, id + "F1", {"entities" : qUnion([Q0, Q1, Q2, Q3, Q4, Q5, Q6, Q7, Q8, Q9, Q10, Q11, Q12, Q13, Q14, Q15, Q16, Q17, Q18, Q19, Q20, Q21, Q22, Q23, Q24, Q25, Q26, Q27, Q28, Q29, Q30, Q31, Q32, Q33, Q34, Q35, Q36, Q37, Q38, Q39, Q40, Q41, Q42, Q43, Q44, Q45, Q46, Q47, Q48, Q49, Q50, Q51, Q52, Q53, Q54, Q55, Q56, Q57]), "depth" : 500 * mm, "offsetDistance" : 25.4 * mm});
        }
        {
            var Q0;
            Q0=makeQuery(id+"F1.opExtrude","CAP_FACE",FACE,{"disambiguationData":[OSD([sQuery(id+"F0.wireOp",EDGE,"E0.bottom"),sQuery(id+"F0.wireOp",EDGE,"E0.top"),sQuery(id+"F0.wireOp",EDGE,"E0.left"),sQuery(id+"F0.wireOp",EDGE,"E0.right"),sQuery(id+"F0.wireOp",EDGE,"E3.bottom"),sQuery(id+"F0.wireOp",EDGE,"E3.top"),sQuery(id+"F0.wireOp",EDGE,"E3.left"),sQuery(id+"F0.wireOp",EDGE,"E3.right"),sQuery(id+"F0.wireOp",EDGE,"E5.left"),sQuery(id+"F0.wireOp",EDGE,"E5.right"),sQuery(id+"F0.wireOp",EDGE,"E8.trimOffspring"),sQuery(id+"F0.wireOp",EDGE,"E12.trimOffspring"),sQuery(id+"F0.wireOp",EDGE,"E16.trimOffspring"),sQuery(id+"F0.wireOp",EDGE,"E20.trimOffspring"),sQuery(id+"F0.wireOp",EDGE,"E24"),sQuery(id+"F0.wireOp",EDGE,"E25"),sQuery(id+"F0.wireOp",EDGE,"E28"),sQuery(id+"F0.wireOp",EDGE,"E29"),sQuery(id+"F0.wireOp",EDGE,"E32"),sQuery(id+"F0.wireOp",EDGE,"E33"),sQuery(id+"F0.wireOp",EDGE,"E36"),sQuery(id+"F0.wireOp",EDGE,"E37"),sQuery(id+"F0.wireOp",EDGE,"E41.bottom"),sQuery(id+"F0.wireOp",EDGE,"E41.top"),sQuery(id+"F0.wireOp",EDGE,"E41.left"),sQuery(id+"F0.wireOp",EDGE,"E41.right"),sQuery(id+"F0.wireOp",EDGE,"E42.bottom"),sQuery(id+"F0.wireOp",EDGE,"E42.top"),sQuery(id+"F0.wireOp",EDGE,"E46"),sQuery(id+"F0.wireOp",EDGE,"E47"),sQuery(id+"F0.wireOp",EDGE,"E48"),sQuery(id+"F0.wireOp",EDGE,"E49"),sQuery(id+"F0.wireOp",EDGE,"E51.trimOffspring"),sQuery(id+"F0.wireOp",EDGE,"E52.trimOffspring"),sQuery(id+"F0.wireOp",EDGE,"E54.trimOffspring"),sQuery(id+"F0.wireOp",EDGE,"E55"),sQuery(id+"F0.wireOp",EDGE,"E56"),sQuery(id+"F0.wireOp",EDGE,"E58.trimOffspring"),sQuery(id+"F0.wireOp",EDGE,"E59.left"),sQuery(id+"F0.wireOp",EDGE,"E59.right"),sQuery(id+"F0.wireOp",EDGE,"E64.trimOffspring"),sQuery(id+"F0.wireOp",EDGE,"E65.trimOffspring"),sQuery(id+"F0.wireOp",EDGE,"E67"),sQuery(id+"F0.wireOp",EDGE,"E68"),sQuery(id+"F0.wireOp",EDGE,"E69"),sQuery(id+"F0.wireOp",EDGE,"E71.trimOffspring"),sQuery(id+"F0.wireOp",EDGE,"E72.trimOffspring"),sQuery(id+"F0.wireOp",EDGE,"E73.trimOffspring"),sQuery(id+"F0.wireOp",EDGE,"E80.filletArc"),sQuery(id+"F0.wireOp",EDGE,"E81.filletArc"),sQuery(id+"F0.wireOp",EDGE,"E82.filletArc"),sQuery(id+"F0.wireOp",EDGE,"E83.filletArc")])],"isStart":false});
            var sketch = newSketch(context, id + "F2", { "sketchPlane" : qUnion([Q0])});
            skLineSegment(sketch, "E84.bottom", {"start": v(6.09, 6.09) * mm, "end": v(-6.09, 6.09) * mm});
            skLineSegment(sketch, "E84.top", {"start": v(6.09, -6.09) * mm, "end": v(-6.09, -6.09) * mm});
            skLineSegment(sketch, "E84.left", {"start": v(6.09, 6.09) * mm, "end": v(6.09, -6.09) * mm});
            skLineSegment(sketch, "E84.right", {"start": v(-6.09, 6.09) * mm, "end": v(-6.09, -6.09) * mm});
            skPoint(sketch, "E84.middle", {"position": v(0, 0) * mm});
            skSolve(sketch);
        }
        {
            var Q0;
            Q0=makeQuery(id+"F2.imprint","IMPRINT",FACE,{"disambiguationData":[TD([[makeQuery(id+"F2.imprint","IMPRINT",EDGE,{"derivedFrom":sQuery(id+"F2.wireOp",EDGE,"E84.bottom")}),1.0]])]});
            extrude(context, id + "F3", {"entities" : qUnion([Q0]), "operationType" : NewBodyOperationType.REMOVE, "endBound" : BoundingType.UP_TO_NEXT, "oppositeDirection" : true, "depth" : 25.4 * mm, "offsetDistance" : 25.4 * mm});
        }
    });
